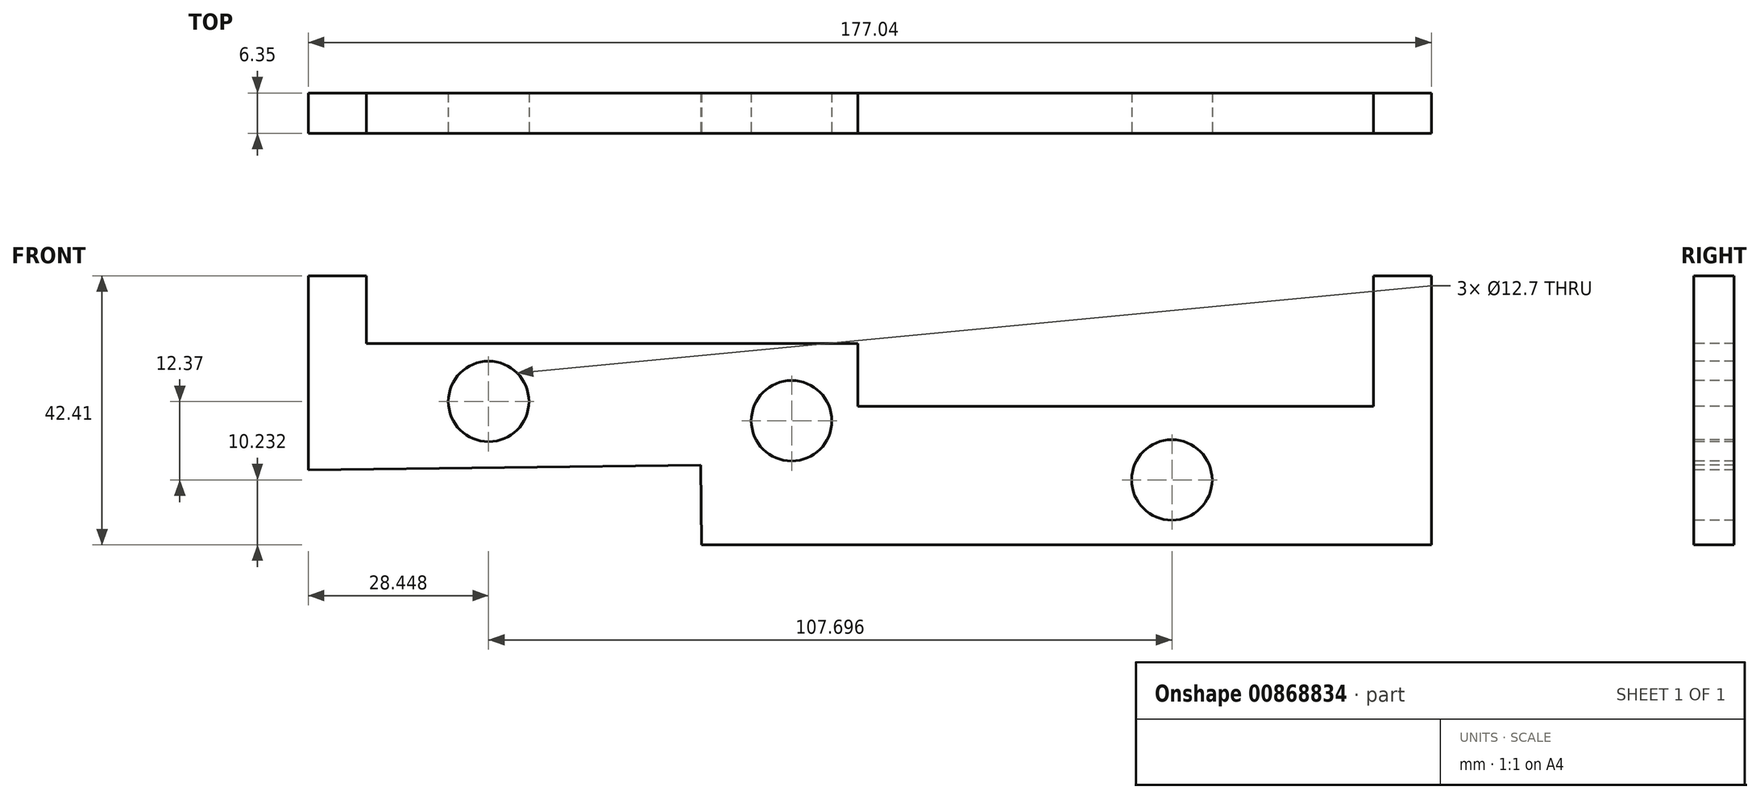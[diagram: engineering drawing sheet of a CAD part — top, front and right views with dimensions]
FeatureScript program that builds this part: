
annotation { "Feature Type Name" : "Feature", "Feature Type Description" : "" }
export const myFeature = defineFeature(function(context is Context, id is Id, definition is map)
    precondition{}
    {
        {
            var Q0;
            Q0=qCreatedBy(makeId("Front.planeOp"),FACE);
            var sketch = newSketch(context, id + "F0", { "sketchPlane" : qUnion([Q0])});
            skLineSegment(sketch, "E0.bottom", {"start": v(0, 0) * mm, "end": v(177.04, 0) * mm});
            skLineSegment(sketch, "E0.top", {"start": v(0, 34.54) * mm, "end": v(177.04, 34.54) * mm});
            skLineSegment(sketch, "E0.left", {"start": v(0, 0) * mm, "end": v(0, 34.54) * mm});
            skLineSegment(sketch, "E0.right", {"start": v(177.04, 0) * mm, "end": v(177.04, 34.54) * mm});
            skSolve(sketch);
        }
        {
            var Q0;
            Q0=makeQuery(id+"F0.imprint","IMPRINT",FACE,{"disambiguationData":[TD([[makeQuery(id+"F0.imprint","IMPRINT",EDGE,{"derivedFrom":sQuery(id+"F0.wireOp",EDGE,"E0.bottom")}),1.0]])]});
            extrude(context, id + "F1", {"entities" : qUnion([Q0]), "depth" : 6.35 * mm, "offsetDistance" : 25.4 * mm});
        }
        {
            var Q0;
            Q0=makeQuery(id+"F1.opExtrude","CAP_FACE",FACE,{"disambiguationData":[OSD([sQuery(id+"F0.wireOp",EDGE,"E0.bottom"),sQuery(id+"F0.wireOp",EDGE,"E0.top"),sQuery(id+"F0.wireOp",EDGE,"E0.left"),sQuery(id+"F0.wireOp",EDGE,"E0.right")])],"isStart":false});
            var sketch = newSketch(context, id + "F2", { "sketchPlane" : qUnion([Q0])});
            skCircle(sketch, "E1", {"center": v(28.45, 14.73) * mm, "radius": 6.35 * mm});
            skCircle(sketch, "E2", {"center": v(76.2, 11.68) * mm, "radius": 6.35 * mm});
            skCircle(sketch, "E3", {"center": v(136.14, 2.36) * mm, "radius": 6.35 * mm});
            skSolve(sketch);
        }
        {
            var Q0;
            Q0=makeQuery(id+"F2.imprint","IMPRINT",FACE,{"disambiguationData":[TD([[makeQuery(id+"F2.imprint","IMPRINT",EDGE,{"derivedFrom":sQuery(id+"F2.wireOp",EDGE,"E1")}),1.0]])]});
            extrude(context, id + "F3", {"entities" : qUnion([Q0]), "operationType" : NewBodyOperationType.REMOVE, "endBound" : BoundingType.THROUGH_ALL, "oppositeDirection" : true, "depth" : 25.4 * mm, "offsetDistance" : 25.4 * mm});
        }
        {
            var Q0;
            Q0 = qSketchRegion(id + "F2", true);
            extrude(context, id + "F4", {"entities" : qUnion([Q0]), "operationType" : NewBodyOperationType.REMOVE, "oppositeDirection" : true, "depth" : 25.4 * mm, "offsetDistance" : 25.4 * mm});
        }
        {
            var Q0;
            Q0=makeQuery(id+"F1.opExtrude","SWEPT_FACE",FACE,{"disambiguationData":[OSD([sQuery(id+"F0.wireOp",EDGE,"E0.bottom")])]});
            var sketch = newSketch(context, id + "F5", { "sketchPlane" : qUnion([Q0])});
            skSolve(sketch);
        }
        {
            var Q0;
            {var subQ0=sQuery(id+"F0.wireOp",EDGE,"E0.bottom");Q0=makeQuery(id+"F5.imprint","IMPRINT",FACE,{"disambiguationData":[TD([[makeQuery(id+"F5.imprint","IMPRINT",EDGE,{"derivedFrom":makeQuery(id+"F1.opExtrude","CAP_EDGE",EDGE,{"disambiguationData":[OSD([subQ0])],"isStart":true})}),1.0]])]});}
            var sketch = newSketch(context, id + "F6", { "sketchPlane" : qUnion([Q0])});
            skLineSegment(sketch, "E4.bottom", {"start": v(0, 0) * mm, "end": v(177.04, 0) * mm});
            skLineSegment(sketch, "E4.top", {"start": v(0, 6.35) * mm, "end": v(177.04, 6.35) * mm});
            skLineSegment(sketch, "E4.left", {"start": v(0, 0) * mm, "end": v(0, 6.35) * mm});
            skLineSegment(sketch, "E4.right", {"start": v(177.04, 0) * mm, "end": v(177.04, 6.35) * mm});
            skSolve(sketch);
        }
        {
            var Q0;
            Q0=makeQuery(id+"F6.imprint","IMPRINT",FACE,{"disambiguationData":[TD([[makeQuery(id+"F6.imprint","IMPRINT",EDGE,{"derivedFrom":sQuery(id+"F6.wireOp",EDGE,"E4.bottom")}),1.0]])]});
            extrude(context, id + "F7", {"entities" : qUnion([Q0]), "operationType" : NewBodyOperationType.ADD, "depth" : 7.87 * mm, "offsetDistance" : 25.4 * mm});
        }
        {
            var Q0;
            Q0=makeQuery(id+"F7.boolean.opBoolean","MERGE",FACE,{"derivedFrom":[makeQuery(id+"F1.opExtrude","CAP_FACE",FACE,{"disambiguationData":[OSD([sQuery(id+"F0.wireOp",EDGE,"E0.bottom"),sQuery(id+"F0.wireOp",EDGE,"E0.top"),sQuery(id+"F0.wireOp",EDGE,"E0.left"),sQuery(id+"F0.wireOp",EDGE,"E0.right")])],"isStart":false}),makeQuery(id+"F7.opExtrude","SWEPT_FACE",FACE,{"disambiguationData":[OSD([sQuery(id+"F6.wireOp",EDGE,"E4.top")])]})]});
            var sketch = newSketch(context, id + "F8", { "sketchPlane" : qUnion([Q0])});
            skCircle(sketch, "E5", {"center": v(136.14, 2.36) * mm, "radius": 6.35 * mm});
            skSolve(sketch);
        }
        {
            var Q0;
            {var subQ1=makeQuery(id+"F7.opExtrude","CAP_EDGE",EDGE,{"disambiguationData":[OSD([sQuery(id+"F6.wireOp",EDGE,"E4.top")])],"isStart":true});Q0=makeQuery(id+"F8.imprint","IMPRINT",FACE,{"disambiguationData":[TD([[makeQuery(id+"F8.imprint","IMPRINT",EDGE,{"derivedFrom":subQ1}),-1.0]])]});}
            extrude(context, id + "F9", {"entities" : qUnion([Q0]), "operationType" : NewBodyOperationType.REMOVE, "oppositeDirection" : true, "depth" : 25.4 * mm, "offsetDistance" : 25.4 * mm});
        }
        {
            var Q0;
            Q0=makeQuery(id+"F7.boolean.opBoolean","MERGE",FACE,{"derivedFrom":[makeQuery(id+"F1.opExtrude","CAP_FACE",FACE,{"disambiguationData":[OSD([sQuery(id+"F0.wireOp",EDGE,"E0.bottom"),sQuery(id+"F0.wireOp",EDGE,"E0.top"),sQuery(id+"F0.wireOp",EDGE,"E0.left"),sQuery(id+"F0.wireOp",EDGE,"E0.right")])],"isStart":false}),makeQuery(id+"F7.opExtrude","SWEPT_FACE",FACE,{"disambiguationData":[OSD([sQuery(id+"F6.wireOp",EDGE,"E4.top")])]})]});
            var sketch = newSketch(context, id + "F10", { "sketchPlane" : qUnion([Q0])});
            skLineSegment(sketch, "E6", {"start": v(9.14, 34.54) * mm, "end": v(9.14, 23.87) * mm});
            skLineSegment(sketch, "E7", {"start": v(9.14, 23.87) * mm, "end": v(86.61, 23.87) * mm});
            skLineSegment(sketch, "E8", {"start": v(86.61, 23.87) * mm, "end": v(86.61, 13.97) * mm});
            skLineSegment(sketch, "E9", {"start": v(86.61, 13.97) * mm, "end": v(167.9, 13.97) * mm});
            skLineSegment(sketch, "E10", {"start": v(167.9, 13.97) * mm, "end": v(167.9, 34.54) * mm});
            skLineSegment(sketch, "E11", {"start": v(167.9, 34.54) * mm, "end": v(9.14, 34.54) * mm});
            skLineSegment(sketch, "E12", {"start": v(61.87, 4.68) * mm, "end": v(62.01, -7.87) * mm});
            skLineSegment(sketch, "E13", {"start": v(62.01, -7.87) * mm, "end": v(-6.4, -8.67) * mm});
            skLineSegment(sketch, "E14", {"start": v(-6.4, -8.67) * mm, "end": v(-6.54, 3.89) * mm});
            skLineSegment(sketch, "E15", {"start": v(61.87, 4.68) * mm, "end": v(-6.6, 3.89) * mm});
            skPoint(sketch, "E16.orphan", {"position": v(-6.6, 9.68) * mm});
            skSolve(sketch);
        }
        {
            var Q0;
            Q0=makeQuery(id+"F10.imprint","IMPRINT",FACE,{"disambiguationData":[TD([[makeQuery(id+"F10.imprint","IMPRINT",EDGE,{"derivedFrom":sQuery(id+"F10.wireOp",EDGE,"E6")}),1.0]])]});
            var Q1;
            {var subQ0=sQuery(id+"F10.wireOp",EDGE,"E12");Q1=makeQuery(id+"F10.imprint","IMPRINT",FACE,{"disambiguationData":[TD([[makeQuery(id+"F10.imprint","IMPRINT",EDGE,{"derivedFrom":subQ0}),-1.0]])]});}
            extrude(context, id + "F11", {"entities" : qUnion([Q0, Q1]), "operationType" : NewBodyOperationType.REMOVE, "oppositeDirection" : true, "depth" : 25.4 * mm, "offsetDistance" : 25.4 * mm});
        }
    });
